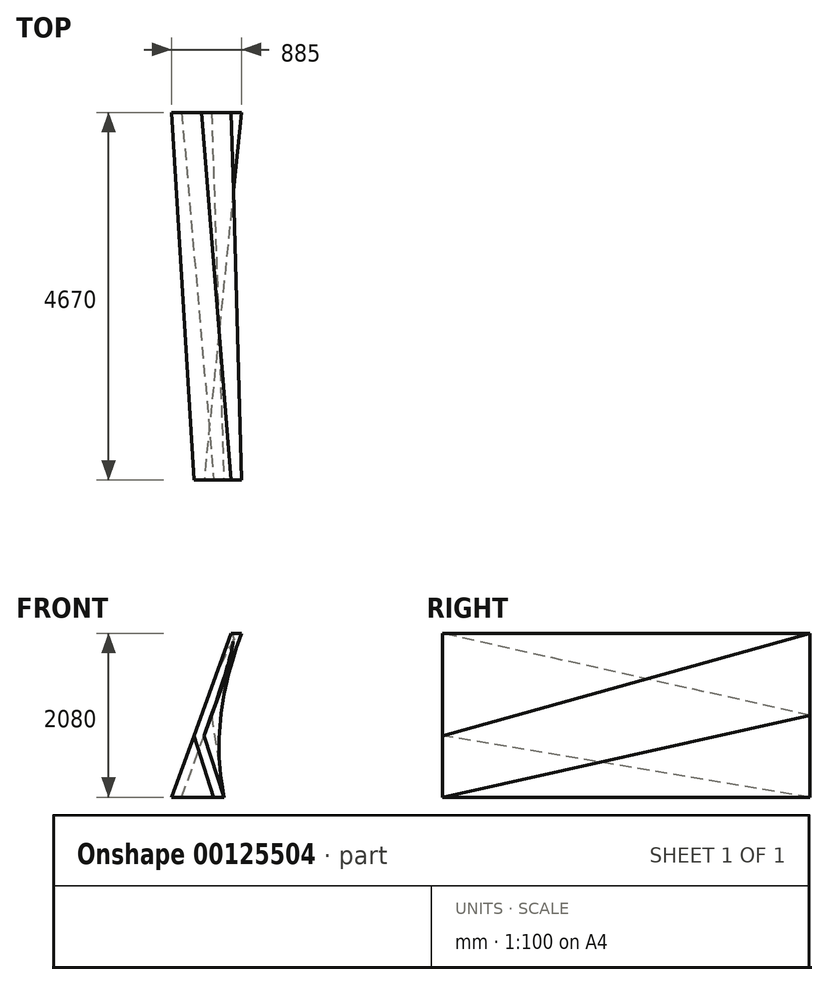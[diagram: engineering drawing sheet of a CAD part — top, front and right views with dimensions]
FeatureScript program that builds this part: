
annotation { "Feature Type Name" : "Feature", "Feature Type Description" : "" }
export const myFeature = defineFeature(function(context is Context, id is Id, definition is map)
    precondition{}
    {
        {
            var Q0;
            Q0=qCreatedBy(makeId("Front.planeOp"),FACE);
            var sketch = newSketch(context, id + "F0", { "sketchPlane" : qUnion([Q0])});
            skLineSegment(sketch, "E0", {"start": v(-1635.36, -3275.85) * mm, "end": v(-1507.36, -3275.85) * mm});
            skLineSegment(sketch, "E1", {"start": v(-1507.36, -3275.85) * mm, "end": v(-750.36, -1195.85) * mm});
            skLineSegment(sketch, "E2", {"start": v(-750.36, -1195.85) * mm, "end": v(-878.36, -1195.85) * mm});
            skLineSegment(sketch, "E3", {"start": v(-878.36, -1195.85) * mm, "end": v(-1635.36, -3275.85) * mm});
            skSolve(sketch);
        }
        {
            var Q0;
            Q0=makeQuery(id+"F0.imprint","IMPRINT",FACE,{"disambiguationData":[TD([[makeQuery(id+"F0.imprint","IMPRINT",EDGE,{"derivedFrom":sQuery(id+"F0.wireOp",EDGE,"E0")}),1.0]])]});
            cPlane(context, id + "F1", {"entities" : qUnion([Q0]), "cplaneType" : CPlaneType.OFFSET, "offset" : 4670 * mm, "width" : 150 * mm, "height" : 150 * mm});
        }
        {
            var Q0;
            Q0=qCreatedBy(id+"F1.planeOp",FACE);
            var sketch = newSketch(context, id + "F2", { "sketchPlane" : qUnion([Q0])});
            skLineSegment(sketch, "E4", {"start": v(-750.36, -1195.85) * mm, "end": v(-878.36, -1195.85) * mm});
            skLineSegment(sketch, "E5", {"start": v(-878.36, -1195.85) * mm, "end": v(-1351.49, -2495.85) * mm});
            skLineSegment(sketch, "E6", {"start": v(-1351.49, -2495.85) * mm, "end": v(-1099.76, -3275.85) * mm});
            skLineSegment(sketch, "E7", {"start": v(-1099.76, -3275.85) * mm, "end": v(-971.76, -3275.85) * mm});
            skLineSegment(sketch, "E8", {"start": v(-971.76, -3275.85) * mm, "end": v(-1223.49, -2495.85) * mm});
            skLineSegment(sketch, "E9", {"start": v(-1223.49, -2495.85) * mm, "end": v(-750.36, -1195.85) * mm});
            skSolve(sketch);
        }
        {
            var Q0;
            Q0 = qSketchRegion(id + "F0", true);
            var Q1;
            Q1 = qSketchRegion(id + "F2", true);
            var Q2;
            Q2=sQuery(id+"F0.wireOp",VERTEX,"E3.end");
            var Q3;
            Q3=sQuery(id+"F2.wireOp",VERTEX,"E6.start");
            loft(context, id + "F3", {"sheetProfilesArray" : [{ "sheetProfileEntities" : qUnion([Q0]) }, { "sheetProfileEntities" : qUnion([Q1]) }], "matchConnections" : true, "connections" : [{ "connectionEntities" : qUnion([Q2, Q3]), "connectionEdgeQueries" : qUnion([]), "connectionEdgeParameters" : [] }]});
        }
    });
